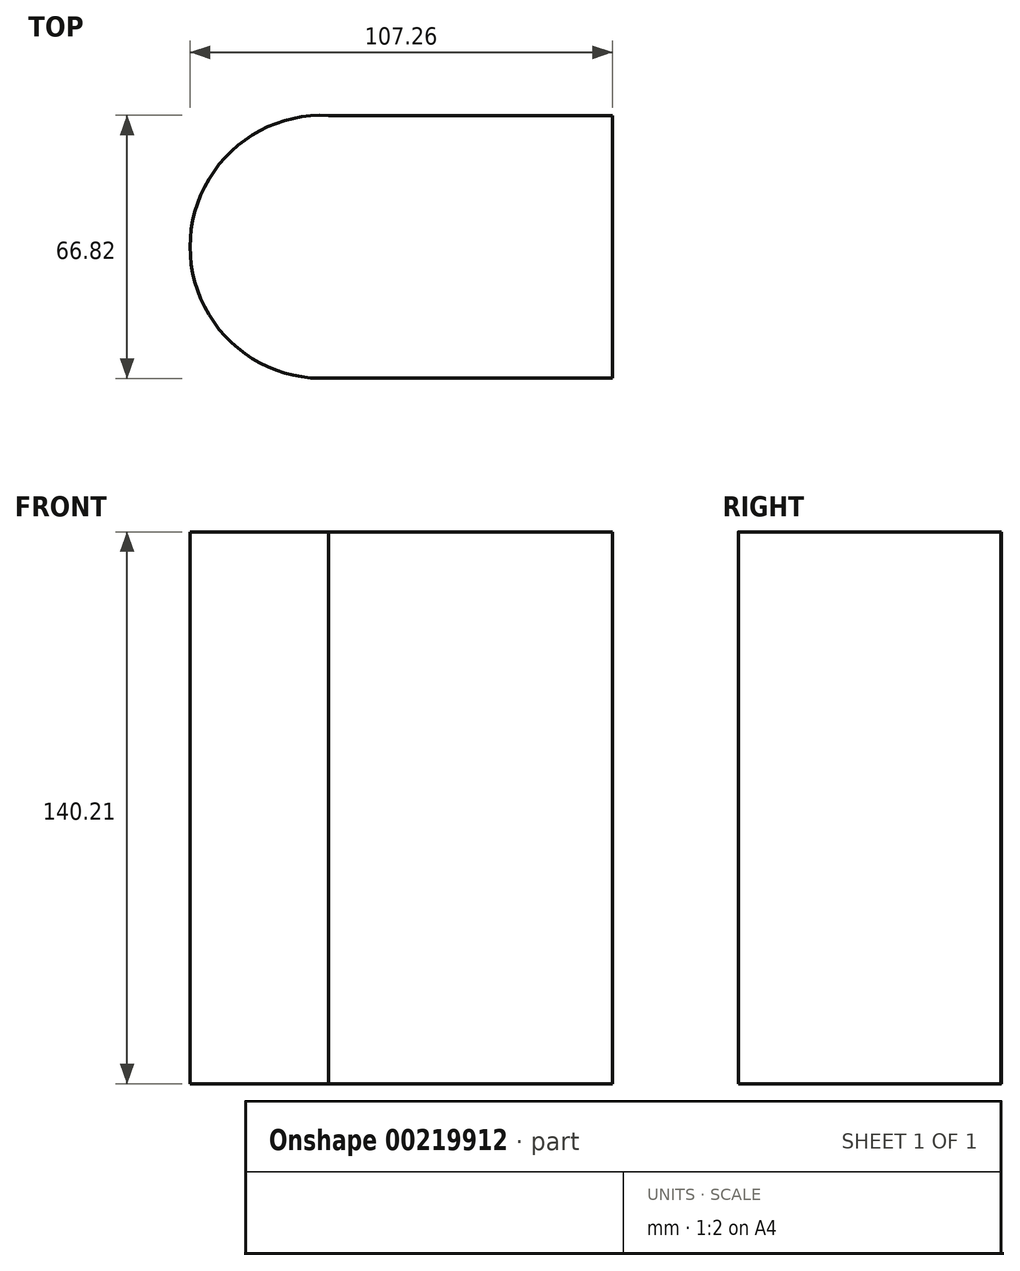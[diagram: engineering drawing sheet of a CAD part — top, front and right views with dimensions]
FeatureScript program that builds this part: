
annotation { "Feature Type Name" : "Feature", "Feature Type Description" : "" }
export const myFeature = defineFeature(function(context is Context, id is Id, definition is map)
    precondition{}
    {
        {
            var Q0;
            Q0=qCreatedBy(makeId("Top.planeOp"),FACE);
            var sketch = newSketch(context, id + "F0", { "sketchPlane" : qUnion([Q0])});
            skArc(sketch, "E0", {"start": v(0, 33.37) * mm, "mid": v(-35.16, 0) * mm, "end": v(0, -33.37) * mm});
            skLineSegment(sketch, "E1", {"start": v(0, 33.37) * mm, "end": v(72.1, 33.37) * mm});
            skLineSegment(sketch, "E2.MirrorCS", {"start": v(0, -33.37) * mm, "end": v(72.1, -33.37) * mm});
            skLineSegment(sketch, "E3", {"start": v(72.1, 33.37) * mm, "end": v(72.1, -33.37) * mm});
            skSolve(sketch);
        }
        {
            var Q0;
            Q0 = qSketchRegion(id + "F0", true);
            extrude(context, id + "F1", {"entities" : qUnion([Q0]), "depth" : 140.2 * mm});
        }
    });
